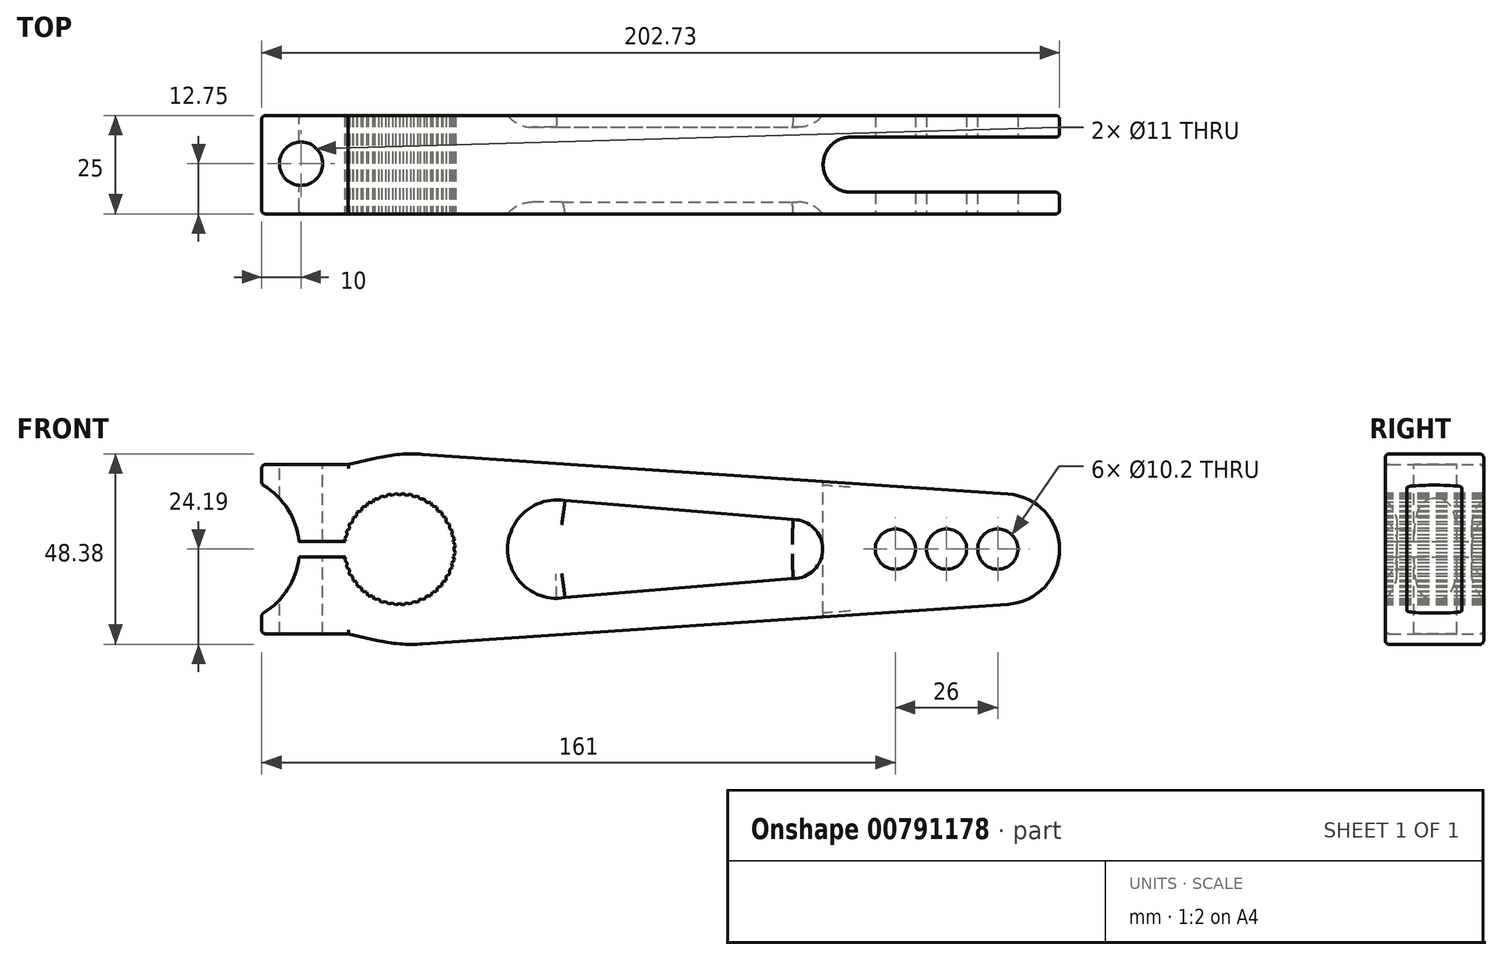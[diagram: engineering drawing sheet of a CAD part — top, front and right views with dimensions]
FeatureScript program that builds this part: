
annotation { "Feature Type Name" : "Feature", "Feature Type Description" : "" }
export const myFeature = defineFeature(function(context is Context, id is Id, definition is map)
    precondition{}
    {
        {
            var Q0;
            Q0=qCreatedBy(makeId("Front.planeOp"),FACE);
            var sketch = newSketch(context, id + "F0", { "sketchPlane" : qUnion([Q0])});
            skLineSegment(sketch, "E0", {"start": v(0, -24.5) * mm, "end": v(154.64, -14) * mm});
            skLineSegment(sketch, "E1", {"start": v(-35, -21.5) * mm, "end": v(-13, -21.5) * mm});
            skLineSegment(sketch, "E2", {"start": v(-13, -21.5) * mm, "end": v(0, -24.5) * mm});
            skLineSegment(sketch, "E3", {"start": v(-35, -21.5) * mm, "end": v(-35, -16.5) * mm});
            skLineSegment(sketch, "E4.MirrorCS", {"start": v(-35, 21.5) * mm, "end": v(-35, 16.5) * mm});
            skLineSegment(sketch, "E5.MirrorCS", {"start": v(0, 24.5) * mm, "end": v(154.64, 14) * mm});
            skLineSegment(sketch, "E6.MirrorCS", {"start": v(-13, 21.5) * mm, "end": v(0, 24.5) * mm});
            skLineSegment(sketch, "E7.MirrorCS", {"start": v(-35, 21.5) * mm, "end": v(-13, 21.5) * mm});
            skArc(sketch, "E8", {"start": v(-35, -16.5) * mm, "mid": v(-25.42, 0) * mm, "end": v(-35, 16.5) * mm});
            skArc(sketch, "E9", {"start": v(154.64, -14) * mm, "mid": v(167.73, 0) * mm, "end": v(154.64, 14) * mm});
            skSolve(sketch);
        }
        {
            var Q0;
            Q0 = qSketchRegion(id + "F0", true);
            extrude(context, id + "F1", {"entities" : qUnion([Q0]), "depth" : 25 * mm, "offsetDistance" : 25 * mm});
        }
        {
            var Q0;
            Q0=makeQuery(id+"F1.opExtrude","CAP_FACE",FACE,{"disambiguationData":[OSD([sQuery(id+"F0.wireOp",EDGE,"E0"),sQuery(id+"F0.wireOp",EDGE,"E1"),sQuery(id+"F0.wireOp",EDGE,"E2"),sQuery(id+"F0.wireOp",EDGE,"E3"),sQuery(id+"F0.wireOp",EDGE,"E4.MirrorCS"),sQuery(id+"F0.wireOp",EDGE,"E5.MirrorCS"),sQuery(id+"F0.wireOp",EDGE,"E6.MirrorCS"),sQuery(id+"F0.wireOp",EDGE,"E7.MirrorCS"),sQuery(id+"F0.wireOp",EDGE,"E8"),sQuery(id+"F0.wireOp",EDGE,"E9")])],"isStart":false});
            var sketch = newSketch(context, id + "F2", { "sketchPlane" : qUnion([Q0])});
            skCircle(sketch, "E10", {"center": v(0, 0) * mm, "radius": 13.75 * mm});
            skSolve(sketch);
        }
        {
            var Q0;
            Q0 = qSketchRegion(id + "F2", true);
            extrude(context, id + "F3", {"entities" : qUnion([Q0]), "operationType" : NewBodyOperationType.REMOVE, "endBound" : BoundingType.THROUGH_ALL, "oppositeDirection" : true, "depth" : 25 * mm, "offsetDistance" : 25 * mm});
        }
        {
            var Q0;
            Q0=makeQuery(id+"F1.opExtrude","CAP_FACE",FACE,{"disambiguationData":[OSD([sQuery(id+"F0.wireOp",EDGE,"E0"),sQuery(id+"F0.wireOp",EDGE,"E1"),sQuery(id+"F0.wireOp",EDGE,"E2"),sQuery(id+"F0.wireOp",EDGE,"E3"),sQuery(id+"F0.wireOp",EDGE,"E4.MirrorCS"),sQuery(id+"F0.wireOp",EDGE,"E5.MirrorCS"),sQuery(id+"F0.wireOp",EDGE,"E6.MirrorCS"),sQuery(id+"F0.wireOp",EDGE,"E7.MirrorCS"),sQuery(id+"F0.wireOp",EDGE,"E8"),sQuery(id+"F0.wireOp",EDGE,"E9")])],"isStart":false});
            var sketch = newSketch(context, id + "F4", { "sketchPlane" : qUnion([Q0])});
            skPoint(sketch, "E11", {"position": v(152, 0) * mm});
            skPoint(sketch, "E12.1.0.0", {"position": v(139, 0) * mm});
            skPoint(sketch, "E12.2.0.0", {"position": v(126, 0) * mm});
            skLineSegment(sketch, "E12.direction1", {"start": v(152, 0) * mm, "end": v(139, 0) * mm, "construction": true});
            skSolve(sketch);
        }
        {
            var Q0;
            Q0=sQuery(id+"F4.wireOp",VERTEX,"E11");
            var Q1;
            Q1=sQuery(id+"F4.wireOp",VERTEX,"E12.1.0.0");
            var Q2;
            Q2=sQuery(id+"F4.wireOp",VERTEX,"E12.2.0.0");
            var Q3;
            Q3=makeQuery(id+"F1.opExtrude","SWEPT_BODY",BODY,{"disambiguationData":[OSD([sQuery(id+"F0.wireOp",EDGE,"E0"),sQuery(id+"F0.wireOp",EDGE,"E1"),sQuery(id+"F0.wireOp",EDGE,"E2"),sQuery(id+"F0.wireOp",EDGE,"E3"),sQuery(id+"F0.wireOp",EDGE,"E4.MirrorCS"),sQuery(id+"F0.wireOp",EDGE,"E5.MirrorCS"),sQuery(id+"F0.wireOp",EDGE,"E6.MirrorCS"),sQuery(id+"F0.wireOp",EDGE,"E7.MirrorCS"),sQuery(id+"F0.wireOp",EDGE,"E8"),sQuery(id+"F0.wireOp",EDGE,"E9")])]});
            hole(context, id + "F5", {"style" : HoleStyle.SIMPLE, "endStyle" : HoleEndStyle.THROUGH, "holeDiameter" : 10.2 * mm, "majorDiameter" : 5 * mm, "tappedDepth" : 12 * mm, "tapClearance" : 3, "startFromSketch" : true, "locations" : qUnion([Q0, Q1, Q2]), "scope" : qUnion([Q3])});
        }
        {
            var Q0;
            Q0=makeQuery(id+"F1.opExtrude","SWEPT_FACE",FACE,{"disambiguationData":[OSD([sQuery(id+"F0.wireOp",EDGE,"E7.MirrorCS")])]});
            var sketch = newSketch(context, id + "F6", { "sketchPlane" : qUnion([Q0])});
            skPoint(sketch, "E13", {"position": v(-25, -12.25) * mm});
            skSolve(sketch);
        }
        {
            var Q0;
            Q0=sQuery(id+"F6.wireOp",VERTEX,"E13");
            var Q1;
            Q1=makeQuery(id+"F1.opExtrude","SWEPT_BODY",BODY,{"disambiguationData":[OSD([sQuery(id+"F0.wireOp",EDGE,"E0"),sQuery(id+"F0.wireOp",EDGE,"E1"),sQuery(id+"F0.wireOp",EDGE,"E2"),sQuery(id+"F0.wireOp",EDGE,"E3"),sQuery(id+"F0.wireOp",EDGE,"E4.MirrorCS"),sQuery(id+"F0.wireOp",EDGE,"E5.MirrorCS"),sQuery(id+"F0.wireOp",EDGE,"E6.MirrorCS"),sQuery(id+"F0.wireOp",EDGE,"E7.MirrorCS"),sQuery(id+"F0.wireOp",EDGE,"E8"),sQuery(id+"F0.wireOp",EDGE,"E9")])]});
            hole(context, id + "F7", {"style" : HoleStyle.SIMPLE, "endStyle" : HoleEndStyle.THROUGH, "standardTappedOrClearance" : lookupTablePath({ "standard" : "ISO", "fit" : "Normal", "size" : "M10", "type" : "Clearance" }), "standardBlindInLast" : lookupTablePath({ "fit" : "Standard", "standard" : "ISO", "size" : "M10", "type" : "Clearance" }), "holeDiameter" : 11 * mm, "majorDiameter" : 5 * mm, "tappedDepth" : 12 * mm, "tapClearance" : 3, "startFromSketch" : true, "locations" : qUnion([Q0]), "scope" : qUnion([Q1])});
        }
        {
            var Q0;
            Q0=qCreatedBy(makeId("Top.planeOp"),FACE);
            cPlane(context, id + "F8", {"entities" : qUnion([Q0]), "cplaneType" : CPlaneType.OFFSET, "offset" : 25 * mm, "width" : 150 * mm, "height" : 150 * mm});
        }
        {
            var Q0;
            Q0=qCreatedBy(id+"F8.planeOp",FACE);
            var sketch = newSketch(context, id + "F9", { "sketchPlane" : qUnion([Q0])});
            skLineSegment(sketch, "E14", {"start": v(114.64, -19.5) * mm, "end": v(219.64, -19.5) * mm});
            skLineSegment(sketch, "E15", {"start": v(114.64, -5.5) * mm, "end": v(219.64, -5.5) * mm});
            skArc(sketch, "E16", {"start": v(114.64, -5.5) * mm, "mid": v(107.64, -12.5) * mm, "end": v(114.64, -19.5) * mm});
            skLineSegment(sketch, "E17", {"start": v(219.64, -5.5) * mm, "end": v(219.64, -19.5) * mm});
            skSolve(sketch);
        }
        {
            var Q0;
            Q0 = qSketchRegion(id + "F9", true);
            extrude(context, id + "F10", {"entities" : qUnion([Q0]), "operationType" : NewBodyOperationType.REMOVE, "endBound" : BoundingType.THROUGH_ALL, "oppositeDirection" : true, "depth" : 25 * mm, "offsetDistance" : 25 * mm});
        }
        {
            var Q0;
            Q0=makeQuery(id+"F1.opExtrude","SWEPT_EDGE",EDGE,{"disambiguationData":[OSD([sQuery(id+"F0.wireOp",EDGE,"E0"),sQuery(id+"F0.wireOp",EDGE,"E2")])]});
            var Q1;
            Q1=makeQuery(id+"F1.opExtrude","SWEPT_EDGE",EDGE,{"disambiguationData":[OSD([sQuery(id+"F0.wireOp",EDGE,"E5.MirrorCS"),sQuery(id+"F0.wireOp",EDGE,"E6.MirrorCS")])]});
            fillet(context, id + "F11", {"entities" : qUnion([Q0, Q1]), "radius" : 40 * mm, "tangentPropagation" : true, "allowEdgeOverflow" : false});
        }
        {
            var Q0;
            Q0=makeQuery(id+"F1.opExtrude","SWEPT_FACE",FACE,{"disambiguationData":[OSD([sQuery(id+"F0.wireOp",EDGE,"E0")])]});
            var Q1;
            Q1=makeQuery(id+"F1.opExtrude","SWEPT_FACE",FACE,{"disambiguationData":[OSD([sQuery(id+"F0.wireOp",EDGE,"E3")])]});
            var Q2;
            Q2=makeQuery(id+"F1.opExtrude","SWEPT_FACE",FACE,{"disambiguationData":[OSD([sQuery(id+"F0.wireOp",EDGE,"E4.MirrorCS")])]});
            var Q3;
            Q3=makeQuery(id+"F1.opExtrude","CAP_EDGE",EDGE,{"disambiguationData":[OSD([sQuery(id+"F0.wireOp",EDGE,"E7.MirrorCS")])],"isStart":false});
            var Q4;
            Q4=makeQuery(id+"F1.opExtrude","CAP_EDGE",EDGE,{"disambiguationData":[OSD([sQuery(id+"F0.wireOp",EDGE,"E7.MirrorCS")])],"isStart":true});
            var Q5;
            Q5=makeQuery(id+"F1.opExtrude","CAP_EDGE",EDGE,{"disambiguationData":[OSD([sQuery(id+"F0.wireOp",EDGE,"E1")])],"isStart":false});
            var Q6;
            Q6=makeQuery(id+"F1.opExtrude","CAP_EDGE",EDGE,{"disambiguationData":[OSD([sQuery(id+"F0.wireOp",EDGE,"E1")])],"isStart":true});
            var Q7;
            {var subQ0=sQuery(id+"F0.wireOp",EDGE,"E8");var subQ1=sQuery(id+"F0.wireOp",EDGE,"E4.MirrorCS");Q7=makeQuery(id+"FzBgPnfZWREcaco_1.boolean.opBoolean","SPLIT",EDGE,{"disambiguationData":[TD([makeQuery(id+"F1.opExtrude","SWEPT_FACE",FACE,{"disambiguationData":[OSD([subQ1])]})])],"derivedFrom":makeQuery(id+"F1.opExtrude","CAP_EDGE",EDGE,{"disambiguationData":[OSD([subQ0])],"isStart":true})});}
            var Q8;
            {var subQ0=sQuery(id+"F0.wireOp",EDGE,"E8");var subQ1=sQuery(id+"F0.wireOp",EDGE,"E4.MirrorCS");Q8=makeQuery(id+"FzBgPnfZWREcaco_1.boolean.opBoolean","SPLIT",EDGE,{"disambiguationData":[TD([makeQuery(id+"F1.opExtrude","SWEPT_FACE",FACE,{"disambiguationData":[OSD([subQ1])]})])],"derivedFrom":makeQuery(id+"F1.opExtrude","CAP_EDGE",EDGE,{"disambiguationData":[OSD([subQ0])],"isStart":false})});}
            var Q9;
            {var subQ0=sQuery(id+"F0.wireOp",EDGE,"E8");var subQ1=sQuery(id+"F0.wireOp",EDGE,"E3");Q9=makeQuery(id+"FzBgPnfZWREcaco_1.boolean.opBoolean","SPLIT",EDGE,{"disambiguationData":[TD([makeQuery(id+"F1.opExtrude","SWEPT_FACE",FACE,{"disambiguationData":[OSD([subQ1])]})])],"derivedFrom":makeQuery(id+"F1.opExtrude","CAP_EDGE",EDGE,{"disambiguationData":[OSD([subQ0])],"isStart":false})});}
            var Q10;
            {var subQ0=sQuery(id+"F0.wireOp",EDGE,"E8");var subQ1=sQuery(id+"F0.wireOp",EDGE,"E3");Q10=makeQuery(id+"FzBgPnfZWREcaco_1.boolean.opBoolean","SPLIT",EDGE,{"disambiguationData":[TD([makeQuery(id+"F1.opExtrude","SWEPT_FACE",FACE,{"disambiguationData":[OSD([subQ1])]})])],"derivedFrom":makeQuery(id+"F1.opExtrude","CAP_EDGE",EDGE,{"disambiguationData":[OSD([subQ0])],"isStart":true})});}
            fillet(context, id + "F12", {"entities" : qUnion([Q0, Q1, Q2, Q3, Q4, Q5, Q6, Q7, Q8, Q9, Q10]), "radius" : 1 * mm, "tangentPropagation" : true, "allowEdgeOverflow" : false});
        }
        {
            var Q0;
            Q0=makeQuery(id+"F1.opExtrude","CAP_FACE",FACE,{"disambiguationData":[OSD([sQuery(id+"F0.wireOp",EDGE,"E0"),sQuery(id+"F0.wireOp",EDGE,"E1"),sQuery(id+"F0.wireOp",EDGE,"E2"),sQuery(id+"F0.wireOp",EDGE,"E3"),sQuery(id+"F0.wireOp",EDGE,"E4.MirrorCS"),sQuery(id+"F0.wireOp",EDGE,"E5.MirrorCS"),sQuery(id+"F0.wireOp",EDGE,"E6.MirrorCS"),sQuery(id+"F0.wireOp",EDGE,"E7.MirrorCS"),sQuery(id+"F0.wireOp",EDGE,"E8"),sQuery(id+"F0.wireOp",EDGE,"E9")])],"isStart":false});
            var sketch = newSketch(context, id + "F13", { "sketchPlane" : qUnion([Q0])});
            skArc(sketch, "E18", {"start": v(42.07, 12.33) * mm, "mid": v(27.5, 0) * mm, "end": v(42.07, -12.33) * mm});
            skArc(sketch, "E19", {"start": v(100, -7.5) * mm, "mid": v(107.5, 0) * mm, "end": v(100, 7.5) * mm});
            skLineSegment(sketch, "E20", {"start": v(40, 12.5) * mm, "end": v(100, 7.5) * mm});
            skLineSegment(sketch, "E21", {"start": v(40, -12.5) * mm, "end": v(100, -7.5) * mm});
            skSolve(sketch);
        }
        {
            var Q0;
            Q0 = qSketchRegion(id + "F13", true);
            extrude(context, id + "F14", {"entities" : qUnion([Q0]), "operationType" : NewBodyOperationType.REMOVE, "oppositeDirection" : true, "depth" : 3 * mm, "offsetDistance" : 25 * mm});
        }
        {
            var Q0;
            Q0=makeQuery(id+"F14.boolean.opBoolean","COPY",EDGE,{"derivedFrom":makeQuery(id+"F14.opExtrude","CAP_EDGE",EDGE,{"disambiguationData":[OSD([sQuery(id+"F13.wireOp",EDGE,"E18")])],"isStart":false})});
            fillet(context, id + "F15", {"entities" : qUnion([Q0]), "radius" : 8 * mm, "tangentPropagation" : true, "allowEdgeOverflow" : false});
        }
        {
            var Q0;
            Q0=makeQuery(id+"F1.opExtrude","CAP_FACE",FACE,{"disambiguationData":[OSD([sQuery(id+"F0.wireOp",EDGE,"E0"),sQuery(id+"F0.wireOp",EDGE,"E1"),sQuery(id+"F0.wireOp",EDGE,"E2"),sQuery(id+"F0.wireOp",EDGE,"E3"),sQuery(id+"F0.wireOp",EDGE,"E4.MirrorCS"),sQuery(id+"F0.wireOp",EDGE,"E5.MirrorCS"),sQuery(id+"F0.wireOp",EDGE,"E6.MirrorCS"),sQuery(id+"F0.wireOp",EDGE,"E7.MirrorCS"),sQuery(id+"F0.wireOp",EDGE,"E8"),sQuery(id+"F0.wireOp",EDGE,"E9")])],"isStart":true});
            var sketch = newSketch(context, id + "F16", { "sketchPlane" : qUnion([Q0])});
            skArc(sketch, "E22", {"start": v(-40, -12.5) * mm, "mid": v(-27.51, 0.52) * mm, "end": v(-41.05, 12.46) * mm});
            skArc(sketch, "E23", {"start": v(-100, 7.5) * mm, "mid": v(-107.5, 0) * mm, "end": v(-100, -7.5) * mm});
            skLineSegment(sketch, "E24", {"start": v(-100, 7.5) * mm, "end": v(-41.05, 12.46) * mm});
            skLineSegment(sketch, "E25", {"start": v(-100, -7.5) * mm, "end": v(-40, -12.5) * mm});
            skPoint(sketch, "E26.orphan", {"position": v(-40, 12.54) * mm});
            skSolve(sketch);
        }
        {
            var Q0;
            Q0 = qSketchRegion(id + "F16", true);
            extrude(context, id + "F17", {"entities" : qUnion([Q0]), "operationType" : NewBodyOperationType.REMOVE, "oppositeDirection" : true, "depth" : 3 * mm, "offsetDistance" : 25 * mm});
        }
        {
            var Q0;
            Q0=makeQuery(id+"F17.boolean.opBoolean","COPY",FACE,{"derivedFrom":makeQuery(id+"F17.opExtrude","CAP_FACE",FACE,{"disambiguationData":[OSD([sQuery(id+"F16.wireOp",EDGE,"E22"),sQuery(id+"F16.wireOp",EDGE,"E23"),sQuery(id+"F16.wireOp",EDGE,"E24"),sQuery(id+"F16.wireOp",EDGE,"E25")])],"isStart":false})});
            fillet(context, id + "F18", {"entities" : qUnion([Q0]), "radius" : 8 * mm, "tangentPropagation" : true, "allowEdgeOverflow" : false});
        }
        {
            var Q0;
            Q0=makeQuery(id+"F1.opExtrude","CAP_FACE",FACE,{"disambiguationData":[OSD([sQuery(id+"F0.wireOp",EDGE,"E0"),sQuery(id+"F0.wireOp",EDGE,"E1"),sQuery(id+"F0.wireOp",EDGE,"E2"),sQuery(id+"F0.wireOp",EDGE,"E3"),sQuery(id+"F0.wireOp",EDGE,"E4.MirrorCS"),sQuery(id+"F0.wireOp",EDGE,"E5.MirrorCS"),sQuery(id+"F0.wireOp",EDGE,"E6.MirrorCS"),sQuery(id+"F0.wireOp",EDGE,"E7.MirrorCS"),sQuery(id+"F0.wireOp",EDGE,"E8"),sQuery(id+"F0.wireOp",EDGE,"E9")])],"isStart":false});
            var sketch = newSketch(context, id + "F19", { "sketchPlane" : qUnion([Q0])});
            skLineSegment(sketch, "E27", {"start": v(0, 13.75) * mm, "end": v(0.93, 14.2) * mm});
            skLineSegment(sketch, "E28", {"start": v(0.93, 14.2) * mm, "end": v(1.8, 13.63) * mm});
            skLineSegment(sketch, "E29", {"start": v(1.8, 13.63) * mm, "end": v(0, 13.75) * mm});
            skLineSegment(sketch, "E30.1.0", {"start": v(-0.93, 14.2) * mm, "end": v(0, 13.75) * mm});
            skLineSegment(sketch, "E30.1.1", {"start": v(-1.8, 13.63) * mm, "end": v(-0.93, 14.2) * mm});
            skLineSegment(sketch, "E30.1.2", {"start": v(0, 13.75) * mm, "end": v(-1.8, 13.63) * mm});
            skLineSegment(sketch, "E30.2.0", {"start": v(-2.78, 13.97) * mm, "end": v(-1.8, 13.63) * mm});
            skLineSegment(sketch, "E30.2.1", {"start": v(-3.56, 13.28) * mm, "end": v(-2.78, 13.97) * mm});
            skLineSegment(sketch, "E30.2.2", {"start": v(-1.8, 13.63) * mm, "end": v(-3.56, 13.28) * mm});
            skLineSegment(sketch, "E30.3.0", {"start": v(-4.58, 13.48) * mm, "end": v(-3.56, 13.28) * mm});
            skLineSegment(sketch, "E30.3.1", {"start": v(-5.26, 12.7) * mm, "end": v(-4.58, 13.48) * mm});
            skLineSegment(sketch, "E30.3.2", {"start": v(-3.56, 13.28) * mm, "end": v(-5.26, 12.7) * mm});
            skLineSegment(sketch, "E30.4.0", {"start": v(-6.3, 12.77) * mm, "end": v(-5.26, 12.7) * mm});
            skLineSegment(sketch, "E30.4.1", {"start": v(-6.87, 11.9) * mm, "end": v(-6.3, 12.77) * mm});
            skLineSegment(sketch, "E30.4.2", {"start": v(-5.26, 12.7) * mm, "end": v(-6.87, 11.9) * mm});
            skLineSegment(sketch, "E30.5.0", {"start": v(-7.91, 11.84) * mm, "end": v(-6.87, 11.9) * mm});
            skLineSegment(sketch, "E30.5.1", {"start": v(-8.37, 10.9) * mm, "end": v(-7.91, 11.84) * mm});
            skLineSegment(sketch, "E30.5.2", {"start": v(-6.88, 11.9) * mm, "end": v(-8.37, 10.9) * mm});
            skLineSegment(sketch, "E30.6.0", {"start": v(-9.39, 10.7) * mm, "end": v(-8.37, 10.9) * mm});
            skLineSegment(sketch, "E30.6.1", {"start": v(-9.72, 9.72) * mm, "end": v(-9.39, 10.7) * mm});
            skLineSegment(sketch, "E30.6.2", {"start": v(-8.37, 10.9) * mm, "end": v(-9.72, 9.72) * mm});
            skLineSegment(sketch, "E30.7.0", {"start": v(-10.7, 9.39) * mm, "end": v(-9.72, 9.72) * mm});
            skLineSegment(sketch, "E30.7.1", {"start": v(-10.9, 8.37) * mm, "end": v(-10.7, 9.39) * mm});
            skLineSegment(sketch, "E30.7.2", {"start": v(-9.72, 9.72) * mm, "end": v(-10.9, 8.37) * mm});
            skLineSegment(sketch, "E30.8.0", {"start": v(-11.84, 7.91) * mm, "end": v(-10.9, 8.37) * mm});
            skLineSegment(sketch, "E30.8.1", {"start": v(-11.9, 6.87) * mm, "end": v(-11.84, 7.91) * mm});
            skLineSegment(sketch, "E30.8.2", {"start": v(-10.9, 8.37) * mm, "end": v(-11.9, 6.87) * mm});
            skLineSegment(sketch, "E30.9.0", {"start": v(-12.77, 6.3) * mm, "end": v(-11.9, 6.87) * mm});
            skLineSegment(sketch, "E30.9.1", {"start": v(-12.7, 5.26) * mm, "end": v(-12.77, 6.3) * mm});
            skLineSegment(sketch, "E30.9.2", {"start": v(-11.9, 6.87) * mm, "end": v(-12.7, 5.26) * mm});
            skLineSegment(sketch, "E30.10.0", {"start": v(-13.48, 4.58) * mm, "end": v(-12.7, 5.26) * mm});
            skLineSegment(sketch, "E30.10.1", {"start": v(-13.28, 3.56) * mm, "end": v(-13.48, 4.58) * mm});
            skLineSegment(sketch, "E30.10.2", {"start": v(-12.7, 5.26) * mm, "end": v(-13.28, 3.56) * mm});
            skLineSegment(sketch, "E30.11.0", {"start": v(-13.97, 2.78) * mm, "end": v(-13.28, 3.56) * mm});
            skLineSegment(sketch, "E30.11.1", {"start": v(-13.63, 1.8) * mm, "end": v(-13.97, 2.78) * mm});
            skLineSegment(sketch, "E30.11.2", {"start": v(-13.28, 3.56) * mm, "end": v(-13.63, 1.8) * mm});
            skLineSegment(sketch, "E30.12.0", {"start": v(-14.2, 0.93) * mm, "end": v(-13.63, 1.8) * mm});
            skLineSegment(sketch, "E30.12.1", {"start": v(-13.75, 0) * mm, "end": v(-14.2, 0.93) * mm});
            skLineSegment(sketch, "E30.12.2", {"start": v(-13.63, 1.8) * mm, "end": v(-13.75, 0) * mm});
            skLineSegment(sketch, "E30.13.0", {"start": v(-14.2, -0.93) * mm, "end": v(-13.75, 0) * mm});
            skLineSegment(sketch, "E30.13.1", {"start": v(-13.63, -1.8) * mm, "end": v(-14.2, -0.93) * mm});
            skLineSegment(sketch, "E30.13.2", {"start": v(-13.75, 0) * mm, "end": v(-13.63, -1.8) * mm});
            skLineSegment(sketch, "E30.14.0", {"start": v(-13.97, -2.78) * mm, "end": v(-13.63, -1.8) * mm});
            skLineSegment(sketch, "E30.14.1", {"start": v(-13.28, -3.56) * mm, "end": v(-13.97, -2.78) * mm});
            skLineSegment(sketch, "E30.14.2", {"start": v(-13.63, -1.8) * mm, "end": v(-13.28, -3.56) * mm});
            skLineSegment(sketch, "E30.15.0", {"start": v(-13.48, -4.58) * mm, "end": v(-13.28, -3.56) * mm});
            skLineSegment(sketch, "E30.15.1", {"start": v(-12.7, -5.26) * mm, "end": v(-13.48, -4.58) * mm});
            skLineSegment(sketch, "E30.15.2", {"start": v(-13.28, -3.56) * mm, "end": v(-12.7, -5.26) * mm});
            skLineSegment(sketch, "E30.16.0", {"start": v(-12.77, -6.3) * mm, "end": v(-12.7, -5.26) * mm});
            skLineSegment(sketch, "E30.16.1", {"start": v(-11.9, -6.87) * mm, "end": v(-12.77, -6.3) * mm});
            skLineSegment(sketch, "E30.16.2", {"start": v(-12.7, -5.26) * mm, "end": v(-11.9, -6.88) * mm});
            skLineSegment(sketch, "E30.17.0", {"start": v(-11.84, -7.91) * mm, "end": v(-11.9, -6.88) * mm});
            skLineSegment(sketch, "E30.17.1", {"start": v(-10.9, -8.37) * mm, "end": v(-11.84, -7.91) * mm});
            skLineSegment(sketch, "E30.17.2", {"start": v(-11.9, -6.88) * mm, "end": v(-10.9, -8.37) * mm});
            skLineSegment(sketch, "E30.18.0", {"start": v(-10.7, -9.39) * mm, "end": v(-10.9, -8.37) * mm});
            skLineSegment(sketch, "E30.18.1", {"start": v(-9.72, -9.72) * mm, "end": v(-10.7, -9.39) * mm});
            skLineSegment(sketch, "E30.18.2", {"start": v(-10.9, -8.37) * mm, "end": v(-9.72, -9.72) * mm});
            skLineSegment(sketch, "E30.19.0", {"start": v(-9.39, -10.7) * mm, "end": v(-9.72, -9.72) * mm});
            skLineSegment(sketch, "E30.19.1", {"start": v(-8.37, -10.9) * mm, "end": v(-9.39, -10.7) * mm});
            skLineSegment(sketch, "E30.19.2", {"start": v(-9.72, -9.72) * mm, "end": v(-8.37, -10.9) * mm});
            skLineSegment(sketch, "E30.20.0", {"start": v(-7.91, -11.84) * mm, "end": v(-8.37, -10.9) * mm});
            skLineSegment(sketch, "E30.20.1", {"start": v(-6.87, -11.9) * mm, "end": v(-7.91, -11.84) * mm});
            skLineSegment(sketch, "E30.20.2", {"start": v(-8.37, -10.9) * mm, "end": v(-6.87, -11.9) * mm});
            skLineSegment(sketch, "E30.21.0", {"start": v(-6.3, -12.77) * mm, "end": v(-6.87, -11.9) * mm});
            skLineSegment(sketch, "E30.21.1", {"start": v(-5.26, -12.7) * mm, "end": v(-6.3, -12.77) * mm});
            skLineSegment(sketch, "E30.21.2", {"start": v(-6.87, -11.9) * mm, "end": v(-5.26, -12.7) * mm});
            skLineSegment(sketch, "E30.22.0", {"start": v(-4.58, -13.48) * mm, "end": v(-5.26, -12.7) * mm});
            skLineSegment(sketch, "E30.22.1", {"start": v(-3.56, -13.28) * mm, "end": v(-4.58, -13.48) * mm});
            skLineSegment(sketch, "E30.22.2", {"start": v(-5.26, -12.7) * mm, "end": v(-3.56, -13.28) * mm});
            skLineSegment(sketch, "E30.23.0", {"start": v(-2.78, -13.97) * mm, "end": v(-3.56, -13.28) * mm});
            skLineSegment(sketch, "E30.23.1", {"start": v(-1.8, -13.63) * mm, "end": v(-2.78, -13.97) * mm});
            skLineSegment(sketch, "E30.23.2", {"start": v(-3.56, -13.28) * mm, "end": v(-1.8, -13.63) * mm});
            skLineSegment(sketch, "E30.24.0", {"start": v(-0.93, -14.2) * mm, "end": v(-1.8, -13.63) * mm});
            skLineSegment(sketch, "E30.24.1", {"start": v(0, -13.75) * mm, "end": v(-0.93, -14.2) * mm});
            skLineSegment(sketch, "E30.24.2", {"start": v(-1.8, -13.63) * mm, "end": v(0, -13.75) * mm});
            skLineSegment(sketch, "E30.25.0", {"start": v(0.93, -14.2) * mm, "end": v(0, -13.75) * mm});
            skLineSegment(sketch, "E30.25.1", {"start": v(1.8, -13.63) * mm, "end": v(0.93, -14.2) * mm});
            skLineSegment(sketch, "E30.25.2", {"start": v(0, -13.75) * mm, "end": v(1.8, -13.63) * mm});
            skLineSegment(sketch, "E30.26.0", {"start": v(2.78, -13.97) * mm, "end": v(1.8, -13.63) * mm});
            skLineSegment(sketch, "E30.26.1", {"start": v(3.56, -13.28) * mm, "end": v(2.78, -13.97) * mm});
            skLineSegment(sketch, "E30.26.2", {"start": v(1.8, -13.63) * mm, "end": v(3.56, -13.28) * mm});
            skLineSegment(sketch, "E30.27.0", {"start": v(4.58, -13.48) * mm, "end": v(3.56, -13.28) * mm});
            skLineSegment(sketch, "E30.27.1", {"start": v(5.26, -12.7) * mm, "end": v(4.58, -13.48) * mm});
            skLineSegment(sketch, "E30.27.2", {"start": v(3.56, -13.28) * mm, "end": v(5.26, -12.7) * mm});
            skLineSegment(sketch, "E30.28.0", {"start": v(6.3, -12.77) * mm, "end": v(5.26, -12.7) * mm});
            skLineSegment(sketch, "E30.28.1", {"start": v(6.88, -11.9) * mm, "end": v(6.3, -12.77) * mm});
            skLineSegment(sketch, "E30.28.2", {"start": v(5.26, -12.7) * mm, "end": v(6.88, -11.9) * mm});
            skLineSegment(sketch, "E30.29.0", {"start": v(7.91, -11.84) * mm, "end": v(6.88, -11.9) * mm});
            skLineSegment(sketch, "E30.29.1", {"start": v(8.37, -10.9) * mm, "end": v(7.91, -11.84) * mm});
            skLineSegment(sketch, "E30.29.2", {"start": v(6.88, -11.9) * mm, "end": v(8.37, -10.9) * mm});
            skLineSegment(sketch, "E30.30.0", {"start": v(9.39, -10.7) * mm, "end": v(8.37, -10.9) * mm});
            skLineSegment(sketch, "E30.30.1", {"start": v(9.72, -9.72) * mm, "end": v(9.39, -10.7) * mm});
            skLineSegment(sketch, "E30.30.2", {"start": v(8.37, -10.9) * mm, "end": v(9.72, -9.72) * mm});
            skLineSegment(sketch, "E30.31.0", {"start": v(10.7, -9.39) * mm, "end": v(9.72, -9.72) * mm});
            skLineSegment(sketch, "E30.31.1", {"start": v(10.9, -8.37) * mm, "end": v(10.7, -9.39) * mm});
            skLineSegment(sketch, "E30.31.2", {"start": v(9.72, -9.72) * mm, "end": v(10.9, -8.37) * mm});
            skLineSegment(sketch, "E30.32.0", {"start": v(11.84, -7.91) * mm, "end": v(10.9, -8.37) * mm});
            skLineSegment(sketch, "E30.32.1", {"start": v(11.9, -6.87) * mm, "end": v(11.84, -7.91) * mm});
            skLineSegment(sketch, "E30.32.2", {"start": v(10.9, -8.37) * mm, "end": v(11.9, -6.87) * mm});
            skLineSegment(sketch, "E30.33.0", {"start": v(12.77, -6.3) * mm, "end": v(11.9, -6.88) * mm});
            skLineSegment(sketch, "E30.33.1", {"start": v(12.7, -5.26) * mm, "end": v(12.77, -6.3) * mm});
            skLineSegment(sketch, "E30.33.2", {"start": v(11.9, -6.87) * mm, "end": v(12.7, -5.26) * mm});
            skLineSegment(sketch, "E30.34.0", {"start": v(13.48, -4.58) * mm, "end": v(12.7, -5.26) * mm});
            skLineSegment(sketch, "E30.34.1", {"start": v(13.28, -3.56) * mm, "end": v(13.48, -4.58) * mm});
            skLineSegment(sketch, "E30.34.2", {"start": v(12.7, -5.26) * mm, "end": v(13.28, -3.56) * mm});
            skLineSegment(sketch, "E30.35.0", {"start": v(13.97, -2.78) * mm, "end": v(13.28, -3.56) * mm});
            skLineSegment(sketch, "E30.35.1", {"start": v(13.63, -1.8) * mm, "end": v(13.97, -2.78) * mm});
            skLineSegment(sketch, "E30.35.2", {"start": v(13.28, -3.56) * mm, "end": v(13.63, -1.8) * mm});
            skLineSegment(sketch, "E30.36.0", {"start": v(14.2, -0.93) * mm, "end": v(13.63, -1.8) * mm});
            skLineSegment(sketch, "E30.36.1", {"start": v(13.75, 0) * mm, "end": v(14.2, -0.93) * mm});
            skLineSegment(sketch, "E30.36.2", {"start": v(13.63, -1.8) * mm, "end": v(13.75, 0) * mm});
            skLineSegment(sketch, "E30.37.0", {"start": v(14.2, 0.93) * mm, "end": v(13.75, 0) * mm});
            skLineSegment(sketch, "E30.37.1", {"start": v(13.63, 1.8) * mm, "end": v(14.2, 0.93) * mm});
            skLineSegment(sketch, "E30.37.2", {"start": v(13.75, 0) * mm, "end": v(13.63, 1.8) * mm});
            skLineSegment(sketch, "E30.38.0", {"start": v(13.97, 2.78) * mm, "end": v(13.63, 1.8) * mm});
            skLineSegment(sketch, "E30.38.1", {"start": v(13.28, 3.56) * mm, "end": v(13.97, 2.78) * mm});
            skLineSegment(sketch, "E30.38.2", {"start": v(13.63, 1.8) * mm, "end": v(13.28, 3.56) * mm});
            skLineSegment(sketch, "E30.39.0", {"start": v(13.48, 4.58) * mm, "end": v(13.28, 3.56) * mm});
            skLineSegment(sketch, "E30.39.1", {"start": v(12.7, 5.26) * mm, "end": v(13.48, 4.58) * mm});
            skLineSegment(sketch, "E30.39.2", {"start": v(13.28, 3.56) * mm, "end": v(12.7, 5.26) * mm});
            skLineSegment(sketch, "E30.40.0", {"start": v(12.77, 6.3) * mm, "end": v(12.7, 5.26) * mm});
            skLineSegment(sketch, "E30.40.1", {"start": v(11.9, 6.87) * mm, "end": v(12.77, 6.3) * mm});
            skLineSegment(sketch, "E30.40.2", {"start": v(12.7, 5.26) * mm, "end": v(11.9, 6.88) * mm});
            skLineSegment(sketch, "E30.41.0", {"start": v(11.84, 7.91) * mm, "end": v(11.9, 6.88) * mm});
            skLineSegment(sketch, "E30.41.1", {"start": v(10.9, 8.37) * mm, "end": v(11.84, 7.91) * mm});
            skLineSegment(sketch, "E30.41.2", {"start": v(11.9, 6.88) * mm, "end": v(10.9, 8.37) * mm});
            skLineSegment(sketch, "E30.42.0", {"start": v(10.7, 9.39) * mm, "end": v(10.9, 8.37) * mm});
            skLineSegment(sketch, "E30.42.1", {"start": v(9.72, 9.72) * mm, "end": v(10.7, 9.39) * mm});
            skLineSegment(sketch, "E30.42.2", {"start": v(10.9, 8.37) * mm, "end": v(9.72, 9.72) * mm});
            skLineSegment(sketch, "E30.43.0", {"start": v(9.39, 10.7) * mm, "end": v(9.72, 9.72) * mm});
            skLineSegment(sketch, "E30.43.1", {"start": v(8.37, 10.9) * mm, "end": v(9.39, 10.7) * mm});
            skLineSegment(sketch, "E30.43.2", {"start": v(9.72, 9.72) * mm, "end": v(8.37, 10.9) * mm});
            skLineSegment(sketch, "E30.44.0", {"start": v(7.91, 11.84) * mm, "end": v(8.37, 10.9) * mm});
            skLineSegment(sketch, "E30.44.1", {"start": v(6.88, 11.9) * mm, "end": v(7.91, 11.84) * mm});
            skLineSegment(sketch, "E30.44.2", {"start": v(8.37, 10.9) * mm, "end": v(6.88, 11.9) * mm});
            skLineSegment(sketch, "E30.45.0", {"start": v(6.3, 12.77) * mm, "end": v(6.88, 11.9) * mm});
            skLineSegment(sketch, "E30.45.1", {"start": v(5.26, 12.7) * mm, "end": v(6.3, 12.77) * mm});
            skLineSegment(sketch, "E30.45.2", {"start": v(6.88, 11.9) * mm, "end": v(5.26, 12.7) * mm});
            skLineSegment(sketch, "E30.46.0", {"start": v(4.58, 13.48) * mm, "end": v(5.26, 12.7) * mm});
            skLineSegment(sketch, "E30.46.1", {"start": v(3.56, 13.28) * mm, "end": v(4.58, 13.48) * mm});
            skLineSegment(sketch, "E30.46.2", {"start": v(5.26, 12.7) * mm, "end": v(3.56, 13.28) * mm});
            skLineSegment(sketch, "E30.47.0", {"start": v(2.78, 13.97) * mm, "end": v(3.56, 13.28) * mm});
            skLineSegment(sketch, "E30.47.1", {"start": v(1.8, 13.63) * mm, "end": v(2.78, 13.97) * mm});
            skLineSegment(sketch, "E30.47.2", {"start": v(3.56, 13.28) * mm, "end": v(1.8, 13.63) * mm});
            skPoint(sketch, "E30.center", {"position": v(0, 0) * mm});
            skSolve(sketch);
        }
        {
            var Q0;
            Q0 = qSketchRegion(id + "F19", true);
            extrude(context, id + "F20", {"entities" : qUnion([Q0]), "operationType" : NewBodyOperationType.REMOVE, "endBound" : BoundingType.THROUGH_ALL, "oppositeDirection" : true, "depth" : 25 * mm, "offsetDistance" : 25 * mm});
        }
        {
            var Q0;
            Q0=makeQuery(id+"F1.opExtrude","CAP_FACE",FACE,{"disambiguationData":[OSD([sQuery(id+"F0.wireOp",EDGE,"E0"),sQuery(id+"F0.wireOp",EDGE,"E1"),sQuery(id+"F0.wireOp",EDGE,"E2"),sQuery(id+"F0.wireOp",EDGE,"E3"),sQuery(id+"F0.wireOp",EDGE,"E4.MirrorCS"),sQuery(id+"F0.wireOp",EDGE,"E5.MirrorCS"),sQuery(id+"F0.wireOp",EDGE,"E6.MirrorCS"),sQuery(id+"F0.wireOp",EDGE,"E7.MirrorCS"),sQuery(id+"F0.wireOp",EDGE,"E8"),sQuery(id+"F0.wireOp",EDGE,"E9")])],"isStart":false});
            var sketch = newSketch(context, id + "F21", { "sketchPlane" : qUnion([Q0])});
            skLineSegment(sketch, "E31.bottom", {"start": v(-5, 2) * mm, "end": v(-35, 2) * mm});
            skLineSegment(sketch, "E31.top", {"start": v(-5, -2) * mm, "end": v(-35, -2) * mm});
            skLineSegment(sketch, "E31.left", {"start": v(-5, 2) * mm, "end": v(-5, -2) * mm});
            skLineSegment(sketch, "E31.right", {"start": v(-35, 2) * mm, "end": v(-35, -2) * mm});
            skPoint(sketch, "E31.middle", {"position": v(-20, 0) * mm});
            skSolve(sketch);
        }
        {
            var Q0;
            Q0 = qSketchRegion(id + "F21", true);
            extrude(context, id + "F22", {"entities" : qUnion([Q0]), "operationType" : NewBodyOperationType.REMOVE, "oppositeDirection" : true, "depth" : 25 * mm, "offsetDistance" : 25 * mm});
        }
    });
